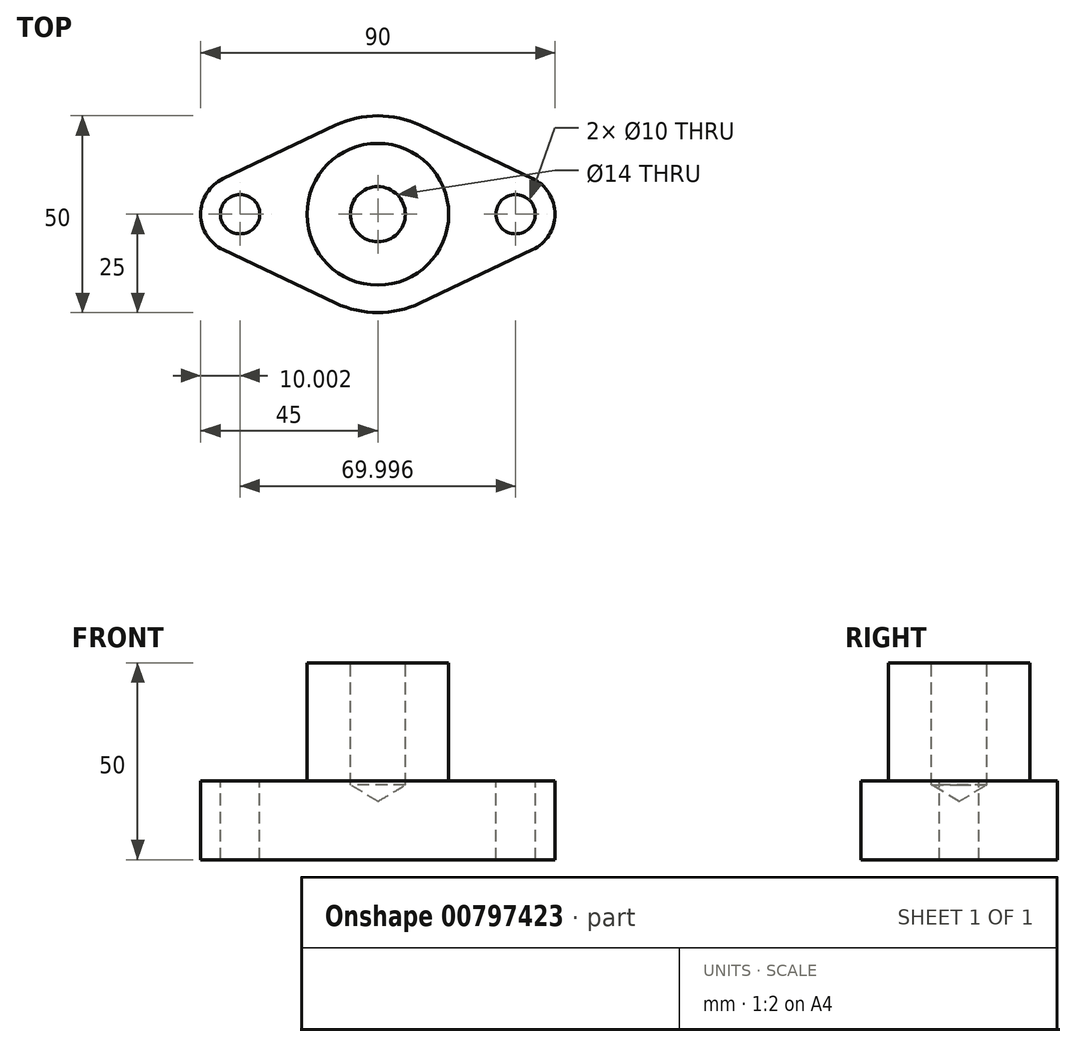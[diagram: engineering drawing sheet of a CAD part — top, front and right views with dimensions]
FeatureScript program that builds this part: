
annotation { "Feature Type Name" : "Feature", "Feature Type Description" : "" }
export const myFeature = defineFeature(function(context is Context, id is Id, definition is map)
    precondition{}
    {
        {
            var Q0;
            Q0=qCreatedBy(makeId("Top.planeOp"),FACE);
            var sketch = newSketch(context, id + "F0", { "sketchPlane" : qUnion([Q0])});
            skLineSegment(sketch, "E0.bottom", {"start": v(0, 0) * mm, "end": v(-58.33, 0) * mm, "construction": true});
            skLineSegment(sketch, "E0.top", {"start": v(0, -27.67) * mm, "end": v(-58.33, -27.67) * mm, "construction": true});
            skLineSegment(sketch, "E0.left", {"start": v(0, 0) * mm, "end": v(0, -27.67) * mm, "construction": true});
            skLineSegment(sketch, "E0.right", {"start": v(-58.33, 0) * mm, "end": v(-58.33, -27.67) * mm, "construction": true});
            skLineSegment(sketch, "E1.0.1.0", {"start": v(0, 27.67) * mm, "end": v(-58.33, 27.67) * mm, "construction": true});
            skLineSegment(sketch, "E1.0.1.1", {"start": v(-58.33, 27.67) * mm, "end": v(-58.33, 0) * mm, "construction": true});
            skLineSegment(sketch, "E1.0.1.3", {"start": v(0, 27.67) * mm, "end": v(0, 0) * mm, "construction": true});
            skLineSegment(sketch, "E1.1.0.0", {"start": v(58.33, 0) * mm, "end": v(0, 0) * mm, "construction": true});
            skLineSegment(sketch, "E1.1.0.2", {"start": v(58.33, -27.67) * mm, "end": v(0, -27.67) * mm, "construction": true});
            skLineSegment(sketch, "E1.1.0.3", {"start": v(58.33, 0) * mm, "end": v(58.33, -27.67) * mm, "construction": true});
            skLineSegment(sketch, "E1.1.1.0", {"start": v(58.33, 27.67) * mm, "end": v(0, 27.67) * mm, "construction": true});
            skLineSegment(sketch, "E1.1.1.1", {"start": v(0, 27.67) * mm, "end": v(0, 0) * mm, "construction": true});
            skLineSegment(sketch, "E1.1.1.2", {"start": v(58.33, 0) * mm, "end": v(0, 0) * mm, "construction": true});
            skLineSegment(sketch, "E1.1.1.3", {"start": v(58.33, 27.67) * mm, "end": v(58.33, 0) * mm, "construction": true});
            skLineSegment(sketch, "E1.direction1", {"start": v(-58.33, 0) * mm, "end": v(0, 0) * mm, "construction": true});
            skLineSegment(sketch, "E1.direction2", {"start": v(-58.33, 0) * mm, "end": v(-58.33, 27.67) * mm, "construction": true});
            skLineSegment(sketch, "E2", {"start": v(-58.33, 0) * mm, "end": v(0, -27.67) * mm});
            skLineSegment(sketch, "E3", {"start": v(0, -27.67) * mm, "end": v(58.33, 0) * mm});
            skLineSegment(sketch, "E4", {"start": v(58.33, 0) * mm, "end": v(0, 27.67) * mm});
            skLineSegment(sketch, "E5", {"start": v(0, 27.67) * mm, "end": v(-58.33, 0) * mm});
            skSolve(sketch);
        }
        {
            var Q0;
            Q0=makeQuery(id+"F0.imprint","IMPRINT",FACE,{"disambiguationData":[TD([[makeQuery(id+"F0.imprint","IMPRINT",EDGE,{"derivedFrom":sQuery(id+"F0.wireOp",EDGE,"E2")}),1.0]])]});
            extrude(context, id + "F1", {"entities" : qUnion([Q0]), "depth" : 20 * mm, "offsetDistance" : 25 * mm});
        }
        {
            var Q0;
            Q0=makeQuery(id+"F1.opExtrude","SWEPT_EDGE",EDGE,{"disambiguationData":[OSD([sQuery(id+"F0.wireOp",EDGE,"E2"),sQuery(id+"F0.wireOp",EDGE,"E5")])]});
            var Q1;
            Q1=makeQuery(id+"F1.opExtrude","SWEPT_EDGE",EDGE,{"disambiguationData":[OSD([sQuery(id+"F0.wireOp",EDGE,"E3"),sQuery(id+"F0.wireOp",EDGE,"E4")])]});
            fillet(context, id + "F2", {"entities" : qUnion([Q0, Q1]), "radius" : 10 * mm, "tangentPropagation" : true, "allowEdgeOverflow" : false});
        }
        {
            var Q0;
            Q0=makeQuery(id+"F1.opExtrude","SWEPT_EDGE",EDGE,{"disambiguationData":[OSD([sQuery(id+"F0.wireOp",EDGE,"E2"),sQuery(id+"F0.wireOp",EDGE,"E3")])]});
            var Q1;
            Q1=makeQuery(id+"F1.opExtrude","SWEPT_EDGE",EDGE,{"disambiguationData":[OSD([sQuery(id+"F0.wireOp",EDGE,"E4"),sQuery(id+"F0.wireOp",EDGE,"E5")])]});
            fillet(context, id + "F3", {"entities" : qUnion([Q0, Q1]), "radius" : 25 * mm, "tangentPropagation" : true, "allowEdgeOverflow" : false});
        }
        {
            var Q0;
            Q0=makeQuery(id+"F1.opExtrude","CAP_FACE",FACE,{"disambiguationData":[OSD([sQuery(id+"F0.wireOp",EDGE,"E2"),sQuery(id+"F0.wireOp",EDGE,"E3"),sQuery(id+"F0.wireOp",EDGE,"E4"),sQuery(id+"F0.wireOp",EDGE,"E5")])],"isStart":false});
            var sketch = newSketch(context, id + "F4", { "sketchPlane" : qUnion([Q0])});
            skPoint(sketch, "E6", {"position": v(35, 0) * mm});
            skPoint(sketch, "E7", {"position": v(0, 0) * mm});
            skPoint(sketch, "E8", {"position": v(-35, 0) * mm});
            skSolve(sketch);
        }
        {
            var Q0;
            Q0=sQuery(id+"F4.wireOp",VERTEX,"E6");
            var Q1;
            Q1=sQuery(id+"F4.wireOp",VERTEX,"E8");
            var Q2;
            Q2=makeQuery(id+"F1.opExtrude","SWEPT_BODY",BODY,{"disambiguationData":[OSD([sQuery(id+"F0.wireOp",EDGE,"E2"),sQuery(id+"F0.wireOp",EDGE,"E3"),sQuery(id+"F0.wireOp",EDGE,"E4"),sQuery(id+"F0.wireOp",EDGE,"E5")])]});
            hole(context, id + "F5", {"style" : HoleStyle.SIMPLE, "endStyle" : HoleEndStyle.THROUGH, "holeDiameter" : 10 * mm, "majorDiameter" : 16 * mm, "isTappedThrough" : true, "tappedDepth" : 25 * mm, "tapClearance" : 3, "startFromSketch" : true, "locations" : qUnion([Q0, Q1]), "scope" : qUnion([Q2])});
        }
        {
            var Q0;
            {var subQ2=sQuery(id+"F0.wireOp",EDGE,"E3");Q0=makeQuery(id+"F4.imprint","IMPRINT",FACE,{"disambiguationData":[TD([[makeQuery(id+"F4.imprint","IMPRINT",EDGE,{"derivedFrom":makeQuery(id+"F1.opExtrude","CAP_EDGE",EDGE,{"disambiguationData":[OSD([subQ2])],"isStart":false})}),1.0]])]});}
            var sketch = newSketch(context, id + "F6", { "sketchPlane" : qUnion([Q0])});
            skCircle(sketch, "E9", {"center": v(0, 0) * mm, "radius": 18 * mm});
            skSolve(sketch);
        }
        {
            var Q0;
            Q0=makeQuery(id+"F6.imprint","IMPRINT",FACE,{"disambiguationData":[TD([[makeQuery(id+"F6.imprint","IMPRINT",EDGE,{"derivedFrom":sQuery(id+"F6.wireOp",EDGE,"E9")}),1.0]])]});
            extrude(context, id + "F7", {"entities" : qUnion([Q0]), "operationType" : NewBodyOperationType.ADD, "depth" : 30 * mm, "offsetDistance" : 25 * mm});
        }
        {
            var Q0;
            Q0=makeQuery(id+"F7.opExtrude","CAP_FACE",FACE,{"disambiguationData":[OSD([sQuery(id+"F6.wireOp",EDGE,"E9")])],"isStart":false});
            var sketch = newSketch(context, id + "F8", { "sketchPlane" : qUnion([Q0])});
            skPoint(sketch, "E10", {"position": v(0, 0) * mm});
            skSolve(sketch);
        }
        {
            var Q0;
            Q0=sQuery(id+"F8.wireOp",VERTEX,"E10");
            var Q1;
            Q1=makeQuery(id+"F1.opExtrude","SWEPT_BODY",BODY,{"disambiguationData":[OSD([sQuery(id+"F0.wireOp",EDGE,"E2"),sQuery(id+"F0.wireOp",EDGE,"E3"),sQuery(id+"F0.wireOp",EDGE,"E4"),sQuery(id+"F0.wireOp",EDGE,"E5")])]});
            hole(context, id + "F9", {"style" : HoleStyle.SIMPLE, "endStyle" : HoleEndStyle.BLIND, "standardTappedOrClearance" : lookupTablePath({ "standard" : "ISO", "engagement" : "75%", "pitch" : "2 mm", "size" : "M16", "type" : "Tapped" }), "standardBlindInLast" : lookupTablePath({ "standard" : "ISO", "engagement" : "75%", "pitch" : "2 mm", "size" : "M16", "type" : "Tapped" }), "holeDiameter" : 14 * mm, "majorDiameter" : 16 * mm, "showTappedDepth" : true, "holeDepth" : 31 * mm, "isTappedThrough" : true, "tappedDepth" : 25 * mm, "tapClearance" : 3, "startFromSketch" : true, "locations" : qUnion([Q0]), "scope" : qUnion([Q1])});
        }
    });
